# Revit family: TESK_Насос вертикальный_SVM(T)-3
name_source: partatom
category: Оборудование
units: mm (PartAtom-declared; Revit-internal decimal feet)

## family parameters
Всегда вертикально = Да
Классификация = Насос
На основе рабочей плоскости = Нет
Общий = Нет
При загрузке вырезать с полостями = Нет
Размер круглого соединителя = Использовать диаметр
Тип детали = Вставляется
Точка расчета площади = Нет

## types (46) — shared parameters
ADSK_Версия Revit = 2019
ADSK_Версия семейства = 1.0
ADSK_Диаметр условный = 25 мм
ADSK_Единица измерения = шт.
ADSK_Завод-изготовитель = TESK
ADSK_Классификация нагрузок = Прочее
ADSK_Количество = 1
ADSK_Количество фаз = 3
ADSK_Количество фаз числовое = 3
ADSK_Коэффициент мощности = 1
ADSK_Наименование краткое = Вертикальный многоступенчатый центробежный насос
ADSK_Напряжение = 400 В
URL = www.teskpump.ru
Длина_ВспомЛиния = 30 мм
Материал_1 = TESK_Черный_Условный
Материал_2 = TESK_Нержавеющая сталь
Материал_КорпусДвигателя = TESK_Черный_Ребра_Условный
Таблица_Поиска = TESK_SVM(T)-3
УГО_Длина = 250 мм
Фланец_Толщина = 18 мм

## per-type parameters (varying)
| type | ADSK_Код изделия | ADSK_Масса | ADSK_Масса_Текст | ADSK_Наименование | ADSK_Номинальная мощность | ADSK_Полная мощность | Высота_Корпуса | Высота_Перехода | Двигатель_Высота | Двигатель_ОтступКоробки | Двигатель_Ширина | Материал_КорпусУлитка | Напор максимальный |
| SVM 3-2 0.37kW 3x380V 50Hz IE3 | 773-20003380NSSF | 20 | 20 | Вертикальный многоступенчатый центробежный насос SVM, DN25, PN25, Hmax=12.5м (3x380V 50Hz IE3) | 0 кВт | 0 кВ·А | 258 мм | 90 мм | 239 мм | 117 мм | 148 мм | TESK_Нержавеющая сталь | 12.5 |
| SVM 3-3 0.37kW 3x380V 50Hz IE3 | 773-30003380NSSF | 20 | 20 | Вертикальный многоступенчатый центробежный насос SVM, DN25, PN25, Hmax=19м (3x380V 50Hz IE3) | 0 кВт | 0 кВ·А | 276 мм | 90 мм | 239 мм | 117 мм | 148 мм | TESK_Нержавеющая сталь | 19 |
| SVM 3-4 0.37kW 3x380V 50Hz IE3 | 773-40003380NSSF | 21 | 21 | Вертикальный многоступенчатый центробежный насос SVM, DN25, PN25, Hmax=25м (3x380V 50Hz IE3) | 0 кВт | 0 кВ·А | 294 мм | 90 мм | 239 мм | 117 мм | 148 мм | TESK_Нержавеющая сталь | 25 |
| SVM 3-5 0.37kW 3x380V 50Hz IE3 | 773-50003380NSSF | 21 | 21 | Вертикальный многоступенчатый центробежный насос SVM, DN25, PN25, Hmax=31м (3x380V 50Hz IE3) | 0 кВт | 0 кВ·А | 312 мм | 90 мм | 239 мм | 117 мм | 148 мм | TESK_Нержавеющая сталь | 31 |
| SVM 3-6 0.55kW 3x380V 50Hz IE3 | 773-60003380NSSF | 23 | 23 | Вертикальный многоступенчатый центробежный насос SVM, DN25, PN25, Hmax=36м (3x380V 50Hz IE3) | 1 кВт | 1 кВ·А | 330 мм | 90 мм | 239 мм | 117 мм | 148 мм | TESK_Нержавеющая сталь | 36 |
| SVM 3-7 0.55kW 3x380V 50Hz IE3 | 773-70003380NSSF | 24 | 24 | Вертикальный многоступенчатый центробежный насос SVM, DN25, PN25, Hmax=43м (3x380V 50Hz IE3) | 1 кВт | 1 кВ·А | 348 мм | 90 мм | 239 мм | 117 мм | 148 мм | TESK_Нержавеющая сталь | 43 |
| SVM 3-8 0.75kW 3x380V 50Hz IE3 | 773-80003380NSSF | 27 | 27 | Вертикальный многоступенчатый центробежный насос SVM, DN25, PN25, Hmax=49м (3x380V 50Hz IE3) | 1 кВт | 1 кВ·А | 376 мм | 110 мм | 280 мм | 142 мм | 170 мм | TESK_Нержавеющая сталь | 49 |
| SVM 3-9 0.75kW 3x380V 50Hz IE3 | 773-90003380NSSF | 28 | 28 | Вертикальный многоступенчатый центробежный насос SVM, DN25, PN25, Hmax=55м (3x380V 50Hz IE3) | 1 кВт | 1 кВ·А | 394 мм | 110 мм | 280 мм | 142 мм | 170 мм | TESK_Нержавеющая сталь | 55 |
| SVM 3-10 0.75kW 3x380V 50Hz IE3 | 773-100003380NSSF | 28 | 28 | Вертикальный многоступенчатый центробежный насос SVM, DN25, PN25, Hmax=61м (3x380V 50Hz IE3) | 1 кВт | 1 кВ·А | 412 мм | 110 мм | 280 мм | 142 мм | 170 мм | TESK_Нержавеющая сталь | 61 |
| SVM 3-11 1.1kW 3x380V 50Hz IE3 | 773-110003380NSSF | 29 | 29 | Вертикальный многоступенчатый центробежный насос SVM, DN25, PN25, Hmax=67м (3x380V 50Hz IE3) | 1 кВт | 1 кВ·А | 430 мм | 110 мм | 280 мм | 142 мм | 170 мм | TESK_Нержавеющая сталь | 67 |
| SVM 3-12 1.1kW 3x380V 50Hz IE3 | 773-120003380NSSF | 30 | 30 | Вертикальный многоступенчатый центробежный насос SVM, DN25, PN25, Hmax=73м (3x380V 50Hz IE3) | 1 кВт | 1 кВ·А | 448 мм | 110 мм | 280 мм | 142 мм | 170 мм | TESK_Нержавеющая сталь | 73 |
| SVM 3-13 1.1kW 3x380V 50Hz IE3 | 773-130003380NSSF | 31 | 31 | Вертикальный многоступенчатый центробежный насос SVM, DN25, PN25, Hmax=78м (3x380V 50Hz IE3) | 1 кВт | 1 кВ·А | 466 мм | 110 мм | 280 мм | 142 мм | 170 мм | TESK_Нержавеющая сталь | 78 |
| SVM 3-15 1.1kW 3x380V 50Hz IE3 | 773-150003380NSSF | 32 | 32 | Вертикальный многоступенчатый центробежный насос SVM, DN25, PN25, Hmax=90м (3x380V 50Hz IE3) | 1 кВт | 1 кВ·А | 502 мм | 110 мм | 280 мм | 142 мм | 170 мм | TESK_Нержавеющая сталь | 90 |
| SVM 3-17 1.5kW 3x380V 50Hz IE3 | 773-170003380NSSF | 38 | 38 | Вертикальный многоступенчатый центробежный насос SVM, DN25, PN25, Hmax=103м (3x380V 50Hz IE3) | 2 кВт | 2 кВ·А | 548 мм | 130 мм | 333 мм | 155 мм | 190 мм | TESK_Нержавеющая сталь | 103 |
| SVM 3-19 1.5kW 3x380V 50Hz IE3 | 773-190003380NSSF | 39 | 39 | Вертикальный многоступенчатый центробежный насос SVM, DN25, PN25, Hmax=115м (3x380V 50Hz IE3) | 2 кВт | 2 кВ·А | 584 мм | 130 мм | 333 мм | 155 мм | 190 мм | TESK_Нержавеющая сталь | 115 |
| SVM 3-21 2.2kW 3x380V 50Hz IE3 | 773-210003380NSSF | 42 | 42 | Вертикальный многоступенчатый центробежный насос SVM, DN25, PN25, Hmax=128м (3x380V 50Hz IE3) | 2 кВт | 2 кВ·А | 620 мм | 130 мм | 333 мм | 155 мм | 190 мм | TESK_Нержавеющая сталь | 128 |
| SVM 3-23 2.2kW 3x380V 50Hz IE3 | 773-230003380NSSF | 43 | 43 | Вертикальный многоступенчатый центробежный насос SVM, DN25, PN25, Hmax=140м (3x380V 50Hz IE3) | 2 кВт | 2 кВ·А | 656 мм | 130 мм | 333 мм | 155 мм | 190 мм | TESK_Нержавеющая сталь | 140 |
| SVM 3-25 2.2kW 3x380V 50Hz IE3 | 773-250003380NSSF | 44 | 44 | Вертикальный многоступенчатый центробежный насос SVM, DN25, PN25, Hmax=151м (3x380V 50Hz IE3) | 2 кВт | 2 кВ·А | 692 мм | 130 мм | 333 мм | 155 мм | 190 мм | TESK_Нержавеющая сталь | 151 |
| SVM 3-27 2.2kW 3x380V 50Hz IE3 | 773-270003380NSSF | 45 | 45 | Вертикальный многоступенчатый центробежный насос SVM, DN25, PN25, Hmax=164м (3x380V 50Hz IE3) | 2 кВт | 2 кВ·А | 728 мм | 130 мм | 333 мм | 155 мм | 190 мм | TESK_Нержавеющая сталь | 164 |
| SVM 3-29 2.2kW 3x380V 50Hz IE3 | 773-290003380NSSF | 46 | 46 | Вертикальный многоступенчатый центробежный насос SVM, DN25, PN25, Hmax=175м (3x380V 50Hz IE3) | 2 кВт | 2 кВ·А | 764 мм | 130 мм | 333 мм | 155 мм | 190 мм | TESK_Нержавеющая сталь | 175 |
| SVM 3-31 3kW 3x380V 50Hz IE3 | 773-310003380NSSF | 54 | 54 | Вертикальный многоступенчатый центробежный насос SVM, DN25, PN25, Hmax=187м (3x380V 50Hz IE3) | 3 кВт | 3 кВ·А | 810 мм | 150 мм | 348 мм | 165 мм | 197 мм | TESK_Нержавеющая сталь | 187 |
| SVM 3-33 3kW 3x380V 50Hz IE3 | 773-330003380NSSF | 55 | 55 | Вертикальный многоступенчатый центробежный насос SVM, DN25, PN25, Hmax=199м (3x380V 50Hz IE3) | 3 кВт | 3 кВ·А | 846 мм | 150 мм | 348 мм | 165 мм | 197 мм | TESK_Нержавеющая сталь | 199 |
| SVM 3-36 3kW 3x380V 50Hz IE3 | 773-360003380NSSF | 57 | 57 | Вертикальный многоступенчатый центробежный насос SVM, DN25, PN25, Hmax=218м (3x380V 50Hz IE3) | 3 кВт | 3 кВ·А | 900 мм | 150 мм | 348 мм | 165 мм | 197 мм | TESK_Нержавеющая сталь | 218 |
| SVMT 3-2 0.37kW 3x380V 50Hz IE3 | 773-20003380N | 20 | 20 | Вертикальный многоступенчатый центробежный насос SVMT, DN25, PN25, Hmax=12.5м (3x380V 50Hz IE3) | 0 кВт | 0 кВ·А | 258 мм | 90 мм | 239 мм | 117 мм | 148 мм | TESK_Черный_Условный | 12.5 |
| SVMT 3-3 0.37kW 3x380V 50Hz IE3 | 773-30003380N | 20 | 20 | Вертикальный многоступенчатый центробежный насос SVMT, DN25, PN25, Hmax=19м (3x380V 50Hz IE3) | 0 кВт | 0 кВ·А | 276 мм | 90 мм | 239 мм | 117 мм | 148 мм | TESK_Черный_Условный | 19 |
| SVMT 3-4 0.37kW 3x380V 50Hz IE3 | 773-40003380N | 21 | 21 | Вертикальный многоступенчатый центробежный насос SVMT, DN25, PN25, Hmax=25м (3x380V 50Hz IE3) | 0 кВт | 0 кВ·А | 294 мм | 90 мм | 239 мм | 117 мм | 148 мм | TESK_Черный_Условный | 25 |
| SVMT 3-5 0.37kW 3x380V 50Hz IE3 | 773-50003380N | 21 | 21 | Вертикальный многоступенчатый центробежный насос SVMT, DN25, PN25, Hmax=31м (3x380V 50Hz IE3) | 0 кВт | 0 кВ·А | 312 мм | 90 мм | 239 мм | 117 мм | 148 мм | TESK_Черный_Условный | 31 |
| SVMT 3-6 0.55kW 3x380V 50Hz IE3 | 773-60003380N | 23 | 23 | Вертикальный многоступенчатый центробежный насос SVMT, DN25, PN25, Hmax=36м (3x380V 50Hz IE3) | 1 кВт | 1 кВ·А | 330 мм | 90 мм | 239 мм | 117 мм | 148 мм | TESK_Черный_Условный | 36 |
| SVMT 3-7 0.55kW 3x380V 50Hz IE3 | 773-70003380N | 24 | 24 | Вертикальный многоступенчатый центробежный насос SVMT, DN25, PN25, Hmax=43м (3x380V 50Hz IE3) | 1 кВт | 1 кВ·А | 348 мм | 90 мм | 239 мм | 117 мм | 148 мм | TESK_Черный_Условный | 43 |
| SVMT 3-8 0.75kW 3x380V 50Hz IE3 | 773-80003380N | 27 | 27 | Вертикальный многоступенчатый центробежный насос SVMT, DN25, PN25, Hmax=49м (3x380V 50Hz IE3) | 1 кВт | 1 кВ·А | 376 мм | 110 мм | 280 мм | 142 мм | 170 мм | TESK_Черный_Условный | 49 |
| SVMT 3-9 0.75kW 3x380V 50Hz IE3 | 773-90003380N | 28 | 28 | Вертикальный многоступенчатый центробежный насос SVMT, DN25, PN25, Hmax=55м (3x380V 50Hz IE3) | 1 кВт | 1 кВ·А | 394 мм | 110 мм | 280 мм | 142 мм | 170 мм | TESK_Черный_Условный | 55 |
| SVMT 3-10 0.75kW 3x380V 50Hz IE3 | 773-100003380N | 28 | 28 | Вертикальный многоступенчатый центробежный насос SVMT, DN25, PN25, Hmax=61м (3x380V 50Hz IE3) | 1 кВт | 1 кВ·А | 412 мм | 110 мм | 280 мм | 142 мм | 170 мм | TESK_Черный_Условный | 61 |
| SVMT 3-11 1.1kW 3x380V 50Hz IE3 | 773-110003380N | 29 | 29 | Вертикальный многоступенчатый центробежный насос SVMT, DN25, PN25, Hmax=67м (3x380V 50Hz IE3) | 1 кВт | 1 кВ·А | 430 мм | 110 мм | 280 мм | 142 мм | 170 мм | TESK_Черный_Условный | 67 |
| SVMT 3-12 1.1kW 3x380V 50Hz IE3 | 773-120003380N | 30 | 30 | Вертикальный многоступенчатый центробежный насос SVMT, DN25, PN25, Hmax=73м (3x380V 50Hz IE3) | 1 кВт | 1 кВ·А | 448 мм | 110 мм | 280 мм | 142 мм | 170 мм | TESK_Черный_Условный | 73 |
| SVMT 3-13 1.1kW 3x380V 50Hz IE3 | 773-130003380N | 31 | 31 | Вертикальный многоступенчатый центробежный насос SVMT, DN25, PN25, Hmax=78м (3x380V 50Hz IE3) | 1 кВт | 1 кВ·А | 466 мм | 110 мм | 280 мм | 142 мм | 170 мм | TESK_Черный_Условный | 78 |
| SVMT 3-15 1.1kW 3x380V 50Hz IE3 | 773-150003380N | 32 | 32 | Вертикальный многоступенчатый центробежный насос SVMT, DN25, PN25, Hmax=90м (3x380V 50Hz IE3) | 1 кВт | 1 кВ·А | 502 мм | 110 мм | 280 мм | 142 мм | 170 мм | TESK_Черный_Условный | 90 |
| SVMT 3-17 1.5kW 3x380V 50Hz IE3 | 773-170003380N | 38 | 38 | Вертикальный многоступенчатый центробежный насос SVMT, DN25, PN25, Hmax=103м (3x380V 50Hz IE3) | 2 кВт | 2 кВ·А | 548 мм | 130 мм | 333 мм | 155 мм | 190 мм | TESK_Черный_Условный | 103 |
| SVMT 3-19 1.5kW 3x380V 50Hz IE3 | 773-190003380N | 39 | 39 | Вертикальный многоступенчатый центробежный насос SVMT, DN25, PN25, Hmax=115м (3x380V 50Hz IE3) | 2 кВт | 2 кВ·А | 584 мм | 130 мм | 333 мм | 155 мм | 190 мм | TESK_Черный_Условный | 115 |
| SVMT 3-21 2.2kW 3x380V 50Hz IE3 | 773-210003380N | 42 | 42 | Вертикальный многоступенчатый центробежный насос SVMT, DN25, PN25, Hmax=128м (3x380V 50Hz IE3) | 2 кВт | 2 кВ·А | 620 мм | 130 мм | 333 мм | 155 мм | 190 мм | TESK_Черный_Условный | 128 |
| SVMT 3-23 2.2kW 3x380V 50Hz IE3 | 773-230003380N | 43 | 43 | Вертикальный многоступенчатый центробежный насос SVMT, DN25, PN25, Hmax=140м (3x380V 50Hz IE3) | 2 кВт | 2 кВ·А | 656 мм | 130 мм | 333 мм | 155 мм | 190 мм | TESK_Черный_Условный | 140 |
| SVMT 3-25 2.2kW 3x380V 50Hz IE3 | 773-250003380N | 44 | 44 | Вертикальный многоступенчатый центробежный насос SVMT, DN25, PN25, Hmax=151м (3x380V 50Hz IE3) | 2 кВт | 2 кВ·А | 692 мм | 130 мм | 333 мм | 155 мм | 190 мм | TESK_Черный_Условный | 151 |
| SVMT 3-27 2.2kW 3x380V 50Hz IE3 | 773-270003380N | 45 | 45 | Вертикальный многоступенчатый центробежный насос SVMT, DN25, PN25, Hmax=164м (3x380V 50Hz IE3) | 2 кВт | 2 кВ·А | 728 мм | 130 мм | 333 мм | 155 мм | 190 мм | TESK_Черный_Условный | 164 |
| SVMT 3-29 2.2kW 3x380V 50Hz IE3 | 773-290003380N | 46 | 46 | Вертикальный многоступенчатый центробежный насос SVMT, DN25, PN25, Hmax=175м (3x380V 50Hz IE3) | 2 кВт | 2 кВ·А | 764 мм | 130 мм | 333 мм | 155 мм | 190 мм | TESK_Черный_Условный | 175 |
| SVMT 3-31 3kW 3x380V 50Hz IE3 | 773-310003380N | 54 | 54 | Вертикальный многоступенчатый центробежный насос SVMT, DN25, PN25, Hmax=187м (3x380V 50Hz IE3) | 3 кВт | 3 кВ·А | 810 мм | 150 мм | 348 мм | 165 мм | 197 мм | TESK_Черный_Условный | 187 |
| SVMT 3-33 3kW 3x380V 50Hz IE3 | 773-330003380N | 55 | 55 | Вертикальный многоступенчатый центробежный насос SVMT, DN25, PN25, Hmax=199м (3x380V 50Hz IE3) | 3 кВт | 3 кВ·А | 846 мм | 150 мм | 348 мм | 165 мм | 197 мм | TESK_Черный_Условный | 199 |
| SVMT 3-36 3kW 3x380V 50Hz IE3 | 773-360003380N | 57 | 57 | Вертикальный многоступенчатый центробежный насос SVMT, DN25, PN25, Hmax=218м (3x380V 50Hz IE3) | 3 кВт | 3 кВ·А | 900 мм | 150 мм | 348 мм | 165 мм | 197 мм | TESK_Черный_Условный | 218 |

note: column(s) folded — value = type name in every type: ADSK_Марка
